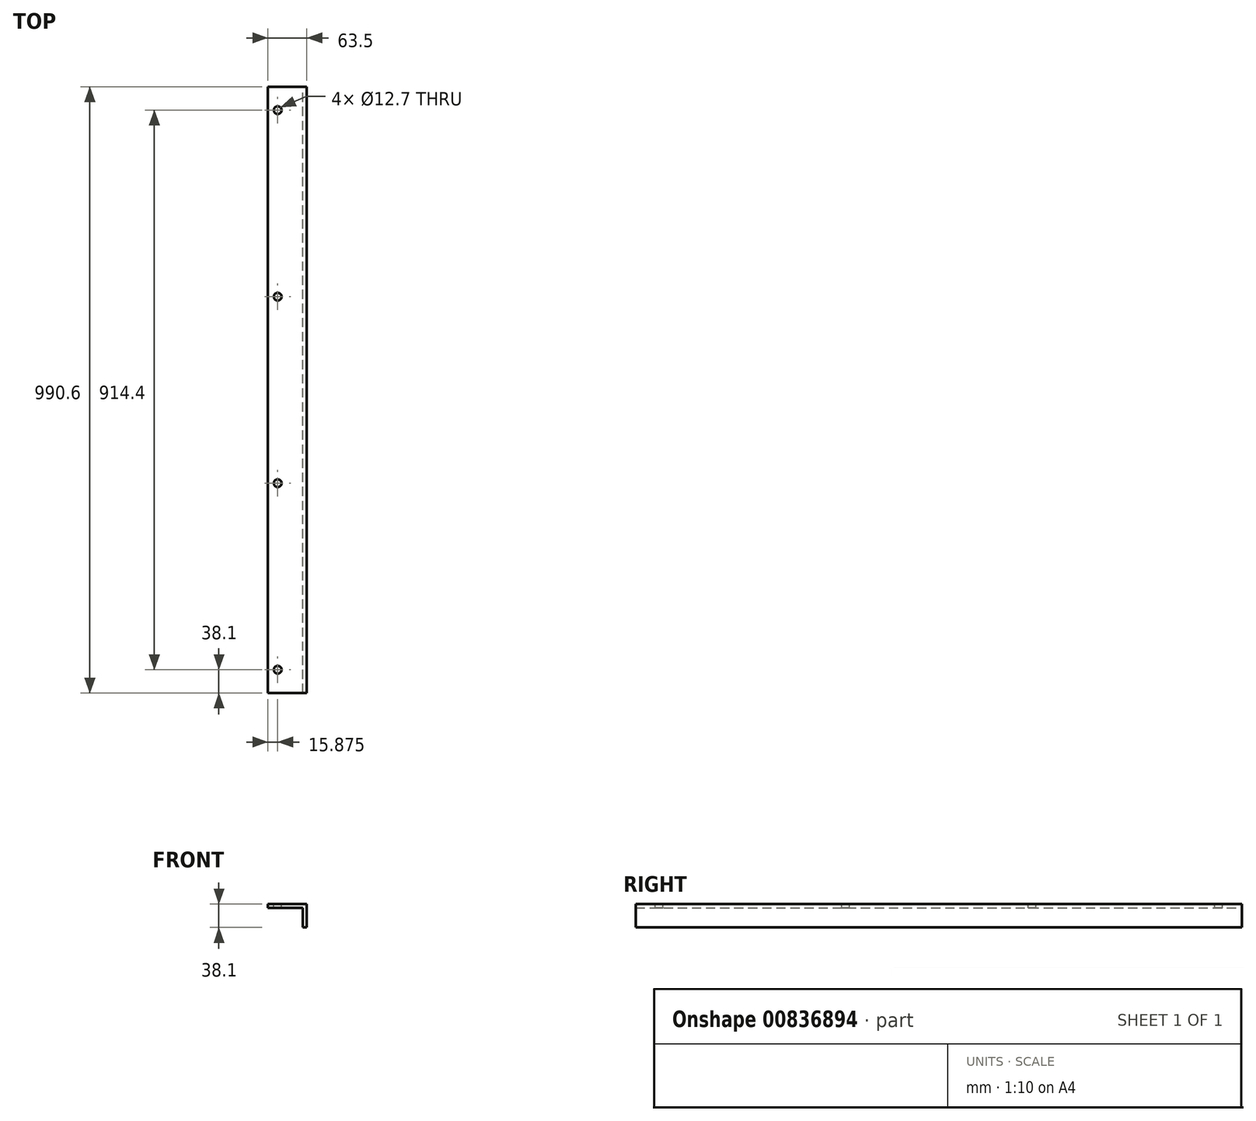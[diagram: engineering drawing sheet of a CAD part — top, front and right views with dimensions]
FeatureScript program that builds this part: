
annotation { "Feature Type Name" : "Feature", "Feature Type Description" : "" }
export const myFeature = defineFeature(function(context is Context, id is Id, definition is map)
    precondition{}
    {
        {
            var Q0;
            Q0=qCreatedBy(makeId("Front.planeOp"),FACE);
            var sketch = newSketch(context, id + "F0", { "sketchPlane" : qUnion([Q0])});
            skLineSegment(sketch, "E0", {"start": v(0, 0) * mm, "end": v(0, 38.1) * mm});
            skLineSegment(sketch, "E1", {"start": v(0, 38.1) * mm, "end": v(-63.5, 38.1) * mm});
            skLineSegment(sketch, "E2", {"start": v(-63.5, 38.1) * mm, "end": v(-63.5, 31.75) * mm});
            skLineSegment(sketch, "E3", {"start": v(-63.5, 31.75) * mm, "end": v(-6.35, 31.75) * mm});
            skLineSegment(sketch, "E4", {"start": v(-6.35, 31.75) * mm, "end": v(-6.35, 0) * mm});
            skLineSegment(sketch, "E5", {"start": v(0, 0) * mm, "end": v(-6.35, 0) * mm});
            skSolve(sketch);
        }
        {
            var Q0;
            Q0 = qSketchRegion(id + "F0", true);
            extrude(context, id + "F1", {"entities" : qUnion([Q0]), "depth" : 990.6 * mm, "offsetDistance" : 25.4 * mm});
        }
        {
            var Q0;
            Q0=makeQuery(id+"F1.opExtrude","SWEPT_FACE",FACE,{"disambiguationData":[OSD([sQuery(id+"F0.wireOp",EDGE,"E1")])]});
            var sketch = newSketch(context, id + "F2", { "sketchPlane" : qUnion([Q0])});
            skCircle(sketch, "E6", {"center": v(-47.62, -952.5) * mm, "radius": 6.35 * mm});
            skCircle(sketch, "E7", {"center": v(-47.62, -647.7) * mm, "radius": 6.35 * mm});
            skCircle(sketch, "E8", {"center": v(-47.62, -342.9) * mm, "radius": 6.35 * mm});
            skCircle(sketch, "E9", {"center": v(-47.62, -38.1) * mm, "radius": 6.35 * mm});
            skLineSegment(sketch, "E10", {"start": v(-47.62, -952.5) * mm, "end": v(-47.62, -647.7) * mm, "construction": true});
            skLineSegment(sketch, "E11", {"start": v(-47.62, -647.7) * mm, "end": v(-47.62, -342.9) * mm, "construction": true});
            skLineSegment(sketch, "E12", {"start": v(-47.62, -342.9) * mm, "end": v(-47.62, -38.1) * mm, "construction": true});
            skSolve(sketch);
        }
        {
            var Q0;
            Q0 = qSketchRegion(id + "F2", true);
            extrude(context, id + "F3", {"entities" : qUnion([Q0]), "operationType" : NewBodyOperationType.REMOVE, "oppositeDirection" : true, "depth" : 25.4 * mm, "offsetDistance" : 25.4 * mm});
        }
    });
